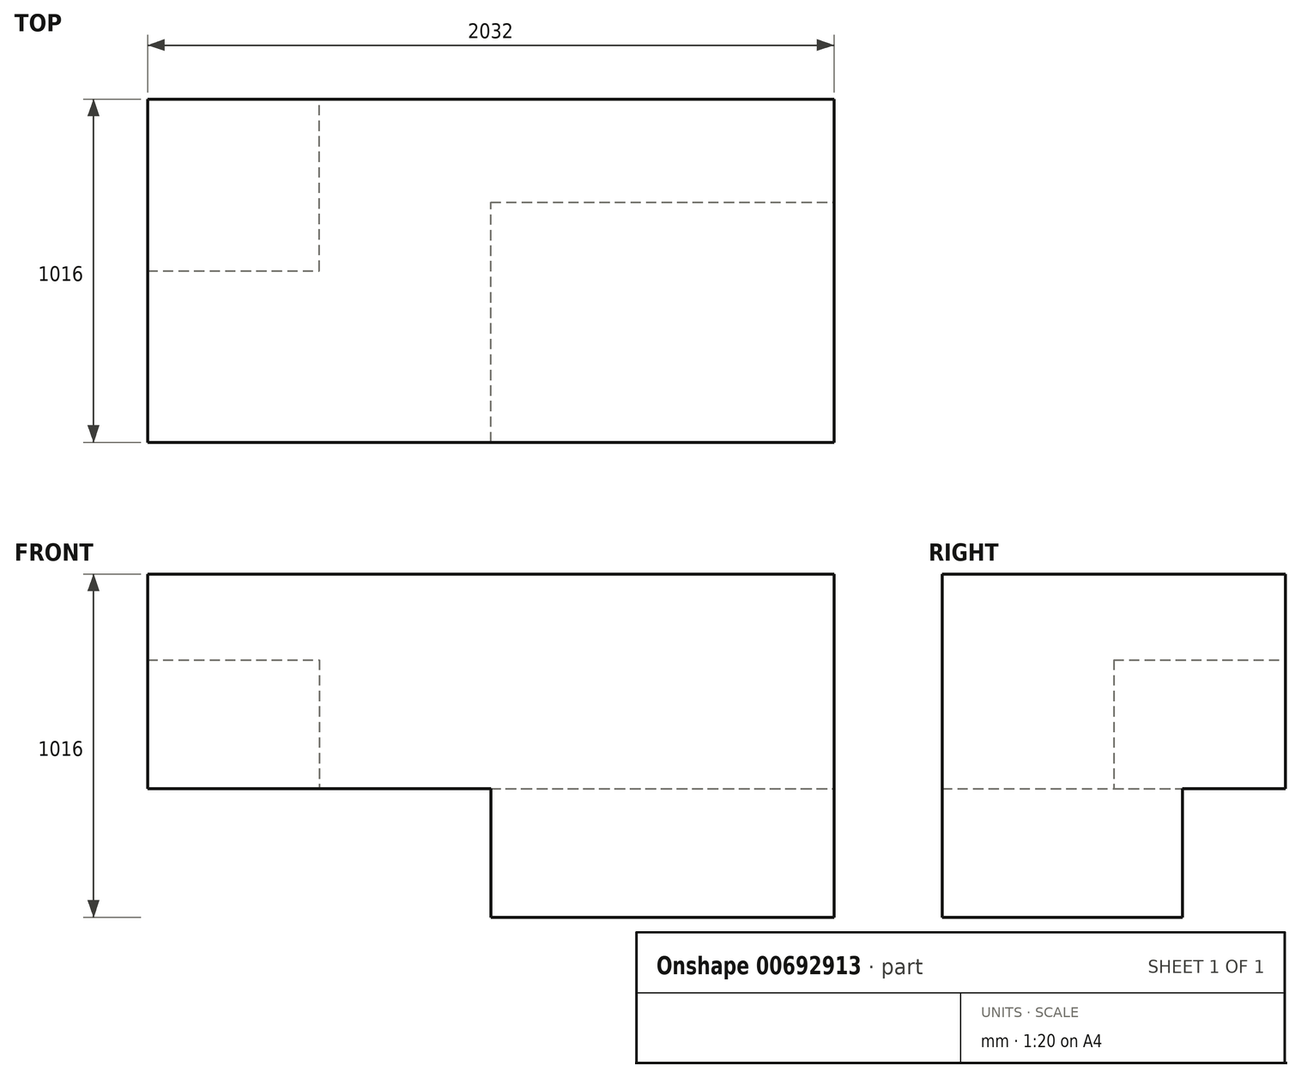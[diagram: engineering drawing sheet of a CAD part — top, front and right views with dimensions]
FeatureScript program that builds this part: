
annotation { "Feature Type Name" : "Feature", "Feature Type Description" : "" }
export const myFeature = defineFeature(function(context is Context, id is Id, definition is map)
    precondition{}
    {
        {
            var Q0;
            Q0=qCreatedBy(makeId("Top.planeOp"),FACE);
            var sketch = newSketch(context, id + "F0", { "sketchPlane" : qUnion([Q0])});
            skLineSegment(sketch, "E0.bottom", {"start": v(-1034.15, -1918.43) * mm, "end": v(997.85, -1918.43) * mm});
            skLineSegment(sketch, "E0.top", {"start": v(-1034.15, -902.43) * mm, "end": v(997.85, -902.43) * mm});
            skLineSegment(sketch, "E0.left", {"start": v(-1034.15, -1918.43) * mm, "end": v(-1034.15, -902.43) * mm});
            skLineSegment(sketch, "E0.right", {"start": v(997.85, -1918.43) * mm, "end": v(997.85, -902.43) * mm});
            skSolve(sketch);
        }
        {
            var Q0;
            Q0 = qSketchRegion(id + "F0", true);
            extrude(context, id + "F1", {"entities" : qUnion([Q0]), "depth" : 635 * mm, "offsetDistance" : 25.4 * mm});
        }
        {
            var Q0;
            Q0=makeQuery(id+"F1.opExtrude","CAP_FACE",FACE,{"disambiguationData":[OSD([sQuery(id+"F0.wireOp",EDGE,"E0.bottom"),sQuery(id+"F0.wireOp",EDGE,"E0.top"),sQuery(id+"F0.wireOp",EDGE,"E0.left"),sQuery(id+"F0.wireOp",EDGE,"E0.right")])],"isStart":true});
            var sketch = newSketch(context, id + "F2", { "sketchPlane" : qUnion([Q0])});
            skPoint(sketch, "E1", {"position": v(-1034.15, 902.43) * mm});
            skPoint(sketch, "E2", {"position": v(-1034.15, 1410.43) * mm});
            skPoint(sketch, "E3", {"position": v(-526.15, 902.43) * mm});
            skPoint(sketch, "E4", {"position": v(-526.15, 1410.43) * mm});
            skLineSegment(sketch, "E5", {"start": v(-1034.15, 1410.43) * mm, "end": v(-526.15, 1410.43) * mm});
            skLineSegment(sketch, "E6", {"start": v(-526.15, 1410.43) * mm, "end": v(-526.15, 902.43) * mm});
            skLineSegment(sketch, "E7", {"start": v(-1034.15, 1410.43) * mm, "end": v(-1034.15, 902.43) * mm});
            skLineSegment(sketch, "E8", {"start": v(-1034.15, 902.43) * mm, "end": v(-526.15, 902.43) * mm});
            skPoint(sketch, "E9", {"position": v(997.85, 1918.43) * mm});
            skPoint(sketch, "E10", {"position": v(-18.15, 1918.43) * mm});
            skPoint(sketch, "E11", {"position": v(-18.15, 1207.23) * mm});
            skPoint(sketch, "E12", {"position": v(997.85, 1207.23) * mm});
            skLineSegment(sketch, "E13", {"start": v(-18.15, 1918.43) * mm, "end": v(997.85, 1918.43) * mm});
            skLineSegment(sketch, "E14", {"start": v(997.85, 1207.23) * mm, "end": v(997.85, 1918.43) * mm});
            skLineSegment(sketch, "E15", {"start": v(-18.15, 1207.23) * mm, "end": v(997.85, 1207.23) * mm});
            skLineSegment(sketch, "E16", {"start": v(-18.15, 1918.43) * mm, "end": v(-18.15, 1207.23) * mm});
            skSolve(sketch);
        }
        {
            var Q0;
            Q0=makeQuery(id+"F2.imprint","IMPRINT",FACE,{"disambiguationData":[TD([[makeQuery(id+"F2.imprint","IMPRINT",EDGE,{"derivedFrom":sQuery(id+"F2.wireOp",EDGE,"E13")}),-1.0]])]});
            extrude(context, id + "F3", {"entities" : qUnion([Q0]), "operationType" : NewBodyOperationType.ADD, "depth" : 381 * mm, "offsetDistance" : 25.4 * mm});
        }
        {
            var Q0;
            Q0=makeQuery(id+"F1.opExtrude","CAP_FACE",FACE,{"disambiguationData":[OSD([sQuery(id+"F0.wireOp",EDGE,"E0.bottom"),sQuery(id+"F0.wireOp",EDGE,"E0.top"),sQuery(id+"F0.wireOp",EDGE,"E0.left"),sQuery(id+"F0.wireOp",EDGE,"E0.right")])],"isStart":true});
            var sketch = newSketch(context, id + "F4", { "sketchPlane" : qUnion([Q0])});
            skLineSegment(sketch, "E17", {"start": v(-1034.15, 1410.43) * mm, "end": v(-526.15, 1410.43) * mm});
            skLineSegment(sketch, "E18", {"start": v(-526.15, 1410.43) * mm, "end": v(-526.15, 902.43) * mm});
            skLineSegment(sketch, "E19", {"start": v(-526.15, 902.43) * mm, "end": v(-1034.15, 902.43) * mm});
            skLineSegment(sketch, "E20", {"start": v(-1034.15, 902.43) * mm, "end": v(-1034.15, 1410.43) * mm});
            skSolve(sketch);
        }
        {
            var Q0;
            Q0=makeQuery(id+"F4.imprint","IMPRINT",FACE,{"disambiguationData":[TD([[makeQuery(id+"F4.imprint","IMPRINT",EDGE,{"derivedFrom":sQuery(id+"F4.wireOp",EDGE,"E17")}),-1.0]])]});
            extrude(context, id + "F5", {"entities" : qUnion([Q0]), "operationType" : NewBodyOperationType.REMOVE, "oppositeDirection" : true, "depth" : 381 * mm, "offsetDistance" : 25.4 * mm});
        }
    });
